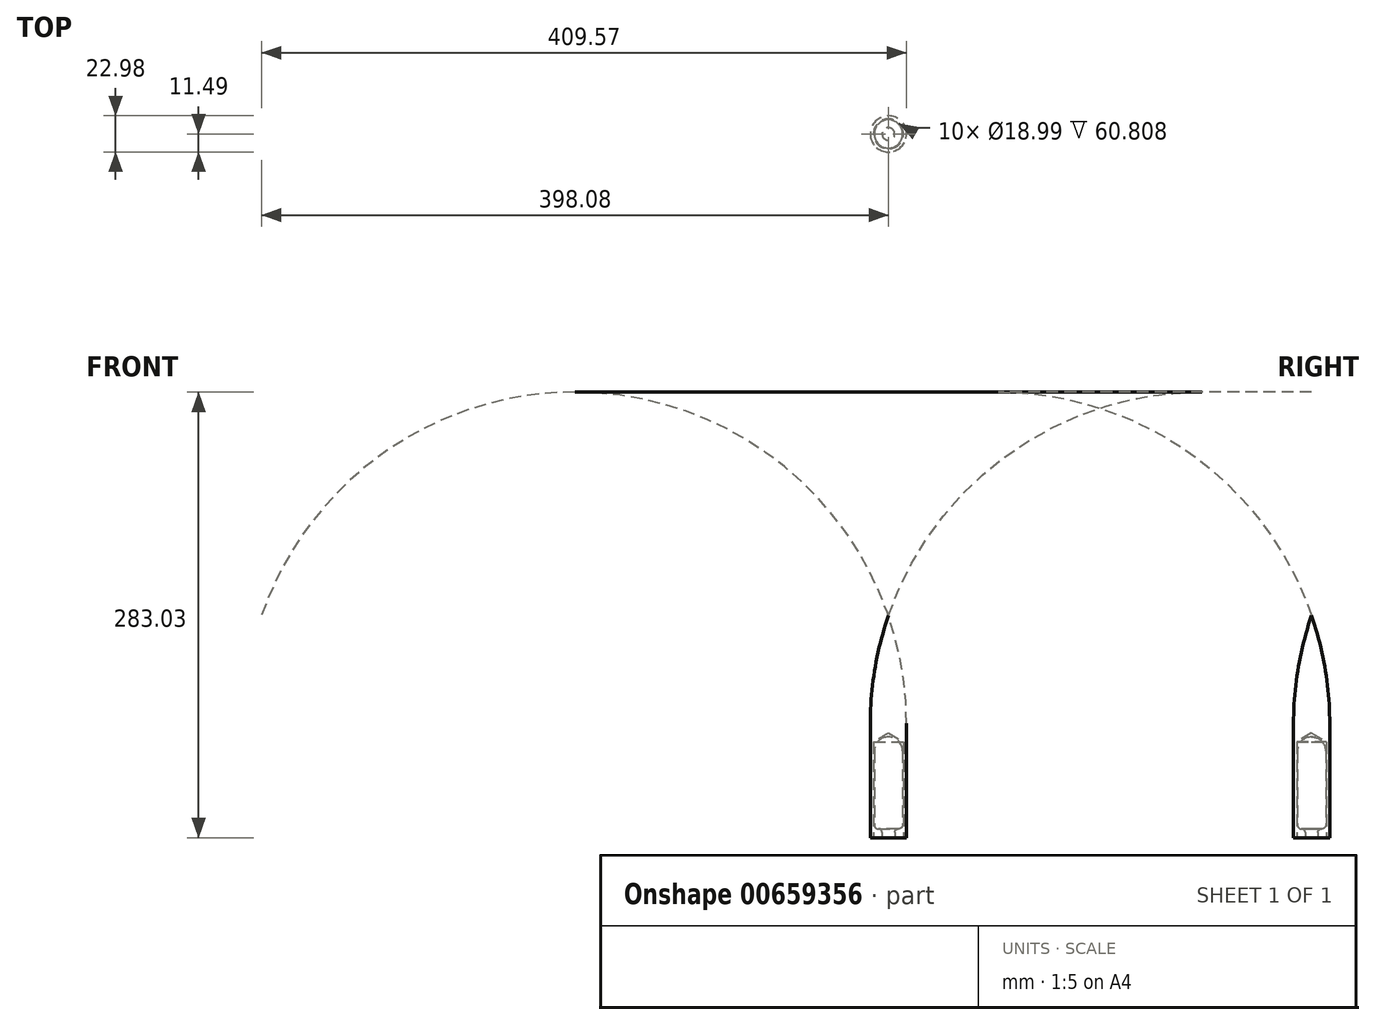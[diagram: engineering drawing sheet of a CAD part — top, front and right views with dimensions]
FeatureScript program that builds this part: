
annotation { "Feature Type Name" : "Feature", "Feature Type Description" : "" }
export const myFeature = defineFeature(function(context is Context, id is Id, definition is map)
    precondition{}
    {
        {
            var Q0;
            Q0=qCreatedBy(makeId("Right.planeOp"),FACE);
            var sketch = newSketch(context, id + "F0", { "sketchPlane" : qUnion([Q0])});
            skLineSegment(sketch, "E0", {"start": v(0, 0) * mm, "end": v(0, 64) * mm});
            skArc(sketch, "E1", {"start": v(9, 55) * mm, "mid": v(6.36, 61.36) * mm, "end": v(0, 64) * mm});
            skLineSegment(sketch, "E2", {"start": v(9, 55) * mm, "end": v(9, 8.13) * mm});
            skArc(sketch, "E3", {"start": v(6.38, 5.6) * mm, "mid": v(8.23, 6.3) * mm, "end": v(9, 8.13) * mm});
            skArc(sketch, "E4", {"start": v(6.38, 5.6) * mm, "mid": v(4.7, 4.95) * mm, "end": v(4, 3.3) * mm});
            skLineSegment(sketch, "E5", {"start": v(4, 3.3) * mm, "end": v(4, 0) * mm});
            skLineSegment(sketch, "E6", {"start": v(4, 0) * mm, "end": v(0, 0) * mm});
            skSolve(sketch);
        }
        {
            var Q0;
            Q0 = qSketchRegion(id + "F0", true);
            var Q1;
            Q1=sQuery(id+"F0.wireOp",EDGE,"E0");
            revolve(context, id + "F1", {"entities" : qUnion([Q0]), "axis" : qUnion([Q1]), "revolveType" : RevolveType.FULL});
        }
        {
            var Q0;
            Q0=qCreatedBy(makeId("Front.planeOp"),FACE);
            var sketch = newSketch(context, id + "F2", { "sketchPlane" : qUnion([Q0])});
            skLineSegment(sketch, "E7", {"start": v(0, 35.82) * mm, "end": v(0, 141.1) * mm});
            skLineSegment(sketch, "E8", {"start": v(11.5, 0) * mm, "end": v(11.5, 35.42) * mm});
            skLineSegment(sketch, "E9", {"start": v(9.5, 31.28) * mm, "end": v(9.5, 0) * mm});
            skLineSegment(sketch, "E10", {"start": v(9.5, 0) * mm, "end": v(11.5, 0) * mm});
            skPoint(sketch, "E11", {"position": v(0, 66.48) * mm});
            skLineSegment(sketch, "E12", {"start": v(0, 66.48) * mm, "end": v(9.5, 60.8) * mm});
            skLineSegment(sketch, "E13", {"start": v(9.5, 60.8) * mm, "end": v(9.5, 31.28) * mm});
            skLineSegment(sketch, "E14", {"start": v(11.5, 35.42) * mm, "end": v(11.5, 72.5) * mm});
            skArc(sketch, "E15", {"start": v(11.5, 72.5) * mm, "mid": v(8.6, 107.28) * mm, "end": v(0, 141.1) * mm});
            skSolve(sketch);
        }
        {
            var Q0;
            Q0 = qSketchRegion(id + "F2", true);
            var Q1;
            Q1=sQuery(id+"F2.wireOp",EDGE,"E7");
            revolve(context, id + "F3", {"entities" : qUnion([Q0]), "axis" : qUnion([Q1]), "revolveType" : RevolveType.FULL});
        }
    });
